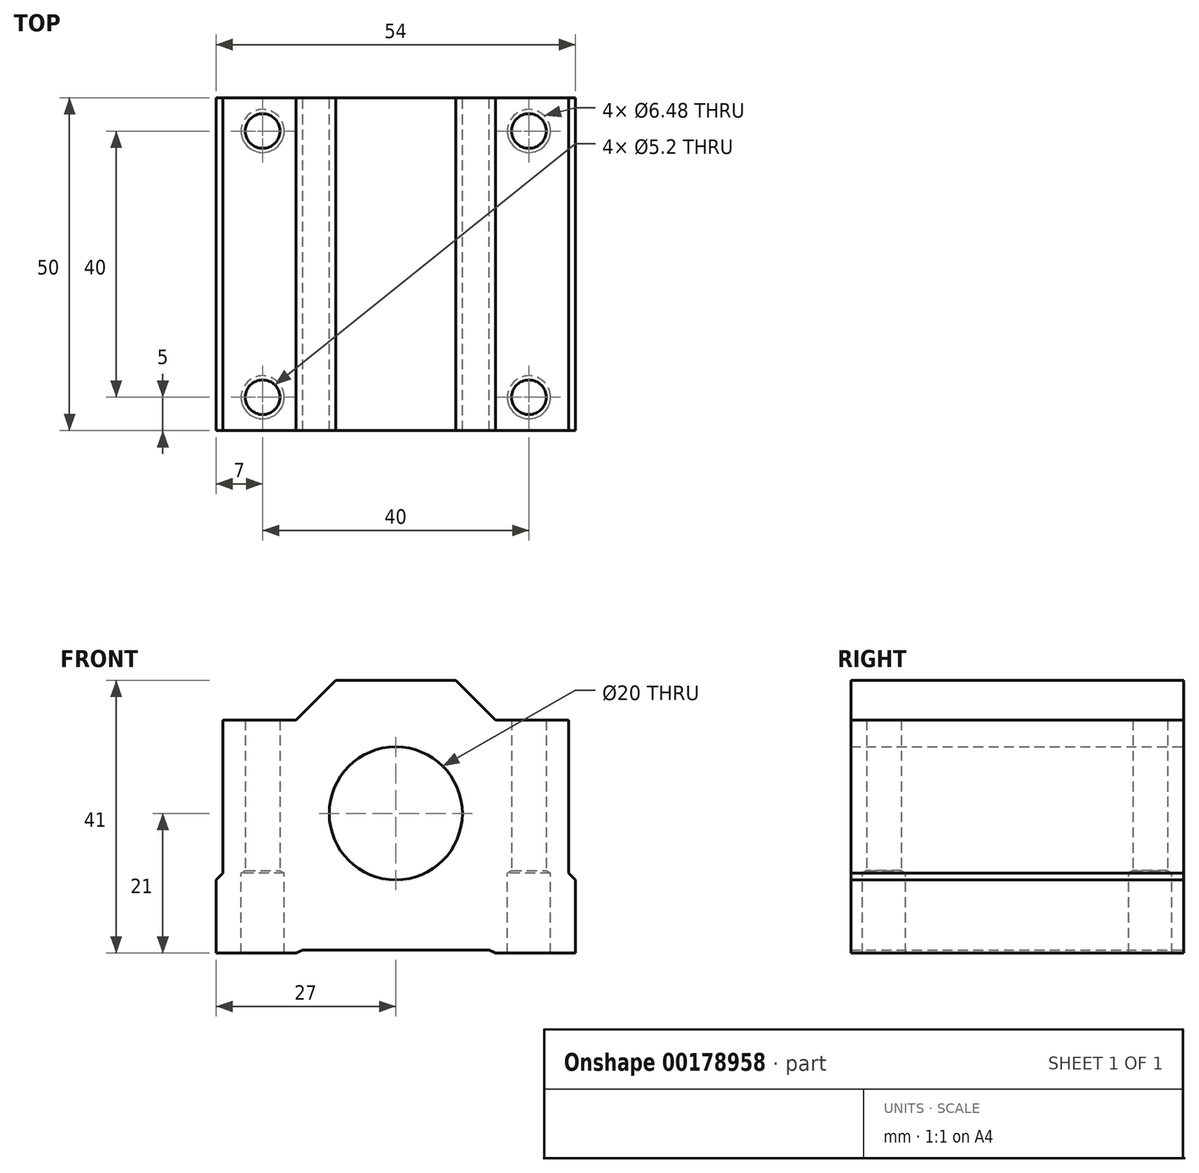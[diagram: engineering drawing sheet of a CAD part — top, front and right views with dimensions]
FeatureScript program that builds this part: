
annotation { "Feature Type Name" : "Feature", "Feature Type Description" : "" }
export const myFeature = defineFeature(function(context is Context, id is Id, definition is map)
    precondition{}
    {
        {
            var Q0;
            Q0=qCreatedBy(makeId("Front.planeOp"),FACE);
            var sketch = newSketch(context, id + "F0", { "sketchPlane" : qUnion([Q0])});
            skLineSegment(sketch, "E0.bottom", {"start": v(27, -20.5) * mm, "end": v(15, -20.5) * mm});
            skLineSegment(sketch, "E0.top", {"start": v(9, 20.5) * mm, "end": v(-9, 20.5) * mm});
            skLineSegment(sketch, "E0.left", {"start": v(27, -20.5) * mm, "end": v(27, -9.5) * mm});
            skLineSegment(sketch, "E0.right", {"start": v(-27, -20.5) * mm, "end": v(-27, -9.5) * mm});
            skPoint(sketch, "E0.middle", {"position": v(0, 0) * mm});
            skCircle(sketch, "E1", {"center": v(0, 0.5) * mm, "radius": 10 * mm});
            skLineSegment(sketch, "E2", {"start": v(-27, 14.5) * mm, "end": v(-15, 14.5) * mm});
            skLineSegment(sketch, "E3", {"start": v(-26, 14.5) * mm, "end": v(-26, -8.5) * mm});
            skLineSegment(sketch, "E4", {"start": v(26, 14.5) * mm, "end": v(26, -8.5) * mm});
            skLineSegment(sketch, "E5", {"start": v(-27, -9.5) * mm, "end": v(-26, -8.5) * mm});
            skLineSegment(sketch, "E6", {"start": v(27, -9.5) * mm, "end": v(26, -8.5) * mm});
            skLineSegment(sketch, "E7", {"start": v(-9, 20.5) * mm, "end": v(-15, 14.5) * mm});
            skLineSegment(sketch, "E8", {"start": v(9, 20.5) * mm, "end": v(15, 14.5) * mm});
            skPoint(sketch, "E9.trimOffspring.end.orphan", {"position": v(-27, 20.5) * mm});
            skPoint(sketch, "E9.trimOffspring.start.orphan", {"position": v(-26, 20.5) * mm});
            skPoint(sketch, "E10.orphan", {"position": v(-27, 0.5) * mm});
            skPoint(sketch, "E11.orphan", {"position": v(-27, -8.5) * mm});
            skPoint(sketch, "E12.orphan", {"position": v(27, 0.5) * mm});
            skLineSegment(sketch, "E13.trimOffspring", {"start": v(0, 0.5) * mm, "end": v(0, 0) * mm});
            skPoint(sketch, "E14.orphan", {"position": v(26, 20.5) * mm});
            skPoint(sketch, "E15.orphan", {"position": v(27, 20.5) * mm});
            skPoint(sketch, "E16.orphan", {"position": v(27, 14.5) * mm});
            skLineSegment(sketch, "E17.trimOffspring", {"start": v(15, 14.5) * mm, "end": v(26, 14.5) * mm});
            skPoint(sketch, "E18.start.orphan", {"position": v(0, 20.5) * mm});
            skPoint(sketch, "E19.trimOffspring.end.orphan", {"position": v(0, -20.5) * mm});
            skLineSegment(sketch, "E20", {"start": v(-14, -20) * mm, "end": v(14, -20) * mm});
            skLineSegment(sketch, "E21", {"start": v(-15, -20.5) * mm, "end": v(-14, -20) * mm});
            skLineSegment(sketch, "E22", {"start": v(15, -20.5) * mm, "end": v(14, -20) * mm});
            skPoint(sketch, "E23.orphan", {"position": v(-27, -20) * mm});
            skLineSegment(sketch, "E24.trimOffspring", {"start": v(-15, -20.5) * mm, "end": v(-27, -20.5) * mm});
            skPoint(sketch, "E25.end.orphan", {"position": v(-14, -20.5) * mm});
            skPoint(sketch, "E26.end.orphan", {"position": v(14, -20.5) * mm});
            skSolve(sketch);
        }
        {
            var Q0;
            Q0=makeQuery(id+"F0.imprint","IMPRINT",FACE,{"disambiguationData":[TD([[makeQuery(id+"F0.imprint","IMPRINT",EDGE,{"derivedFrom":sQuery(id+"F0.wireOp",EDGE,"E0.bottom")}),-1.0]])]});
            extrude(context, id + "F1", {"entities" : qUnion([Q0]), "depth" : 50 * mm});
        }
        {
            var Q0;
            Q0=makeQuery(id+"F1.opExtrude","SWEPT_FACE",FACE,{"disambiguationData":[OSD([sQuery(id+"F0.wireOp",EDGE,"E0.bottom")])]});
            var sketch = newSketch(context, id + "F2", { "sketchPlane" : qUnion([Q0])});
            skCircle(sketch, "E27", {"center": v(20, 5) * mm, "radius": 3.24 * mm});
            skCircle(sketch, "E28", {"center": v(-20, 5) * mm, "radius": 3.24 * mm});
            skCircle(sketch, "E29", {"center": v(20, 45) * mm, "radius": 3.24 * mm});
            skCircle(sketch, "E30", {"center": v(-20, 45) * mm, "radius": 3.24 * mm});
            skPoint(sketch, "E31.start.orphan", {"position": v(27, 5) * mm});
            skPoint(sketch, "E32.start.orphan", {"position": v(27, 45) * mm});
            skPoint(sketch, "E33.orphan", {"position": v(20, 50) * mm});
            skPoint(sketch, "E34.start.orphan", {"position": v(34, 50) * mm});
            skPoint(sketch, "E35.trimOffspring.end.orphan", {"position": v(-27, 45) * mm});
            skPoint(sketch, "E36.orphan", {"position": v(-27, 5) * mm});
            skSolve(sketch);
        }
        {
            var Q0;
            Q0=makeQuery(id+"F1.opExtrude","SWEPT_FACE",FACE,{"disambiguationData":[OSD([sQuery(id+"F0.wireOp",EDGE,"E2")])]});
            var sketch = newSketch(context, id + "F3", { "sketchPlane" : qUnion([Q0])});
            skCircle(sketch, "E37", {"center": v(-20, -45) * mm, "radius": 2.6 * mm});
            skCircle(sketch, "E38", {"center": v(-20, -5) * mm, "radius": 2.6 * mm});
            skPoint(sketch, "E39.orphan", {"position": v(-26, -5) * mm});
            skPoint(sketch, "E40.start.orphan", {"position": v(-20, 0) * mm});
            skPoint(sketch, "E41.start.orphan", {"position": v(-26, -45) * mm});
            skSolve(sketch);
        }
        {
            var Q0;
            Q0=makeQuery(id+"F1.opExtrude","SWEPT_FACE",FACE,{"disambiguationData":[OSD([sQuery(id+"F0.wireOp",EDGE,"E17.trimOffspring")])]});
            var sketch = newSketch(context, id + "F4", { "sketchPlane" : qUnion([Q0])});
            skCircle(sketch, "E42", {"center": v(20, -45) * mm, "radius": 2.6 * mm});
            skCircle(sketch, "E43", {"center": v(20, -5) * mm, "radius": 2.6 * mm});
            skPoint(sketch, "E44.orphan", {"position": v(20, -50) * mm});
            skPoint(sketch, "E45.trimOffspring.end.orphan", {"position": v(26, -45) * mm});
            skPoint(sketch, "E46.trimOffspring.end.orphan", {"position": v(26, -5) * mm});
            skSolve(sketch);
        }
        {
            var Q0;
            Q0=sQuery(id+"F2.wireOp",VERTEX,"E29.center");
            var Q1;
            Q1=makeQuery(id+"F1.opExtrude","SWEPT_BODY",BODY,{"disambiguationData":[OSD([sQuery(id+"F0.wireOp",EDGE,"E0.bottom"),sQuery(id+"F0.wireOp",EDGE,"E0.top"),sQuery(id+"F0.wireOp",EDGE,"E0.left"),sQuery(id+"F0.wireOp",EDGE,"E0.right"),sQuery(id+"F0.wireOp",EDGE,"E1"),sQuery(id+"F0.wireOp",EDGE,"E2"),sQuery(id+"F0.wireOp",EDGE,"E3"),sQuery(id+"F0.wireOp",EDGE,"E4"),sQuery(id+"F0.wireOp",EDGE,"E5"),sQuery(id+"F0.wireOp",EDGE,"E6"),sQuery(id+"F0.wireOp",EDGE,"E7"),sQuery(id+"F0.wireOp",EDGE,"E8"),sQuery(id+"F0.wireOp",EDGE,"E17.trimOffspring")])]});
            hole(context, id + "F5", {"style" : HoleStyle.SIMPLE, "endStyle" : HoleEndStyle.BLIND, "holeDiameter" : 6.48 * mm, "holeDepth" : 12 * mm, "locations" : qUnion([Q0]), "scope" : qUnion([Q1])});
        }
        {
            var Q0;
            Q0=sQuery(id+"F2.wireOp",VERTEX,"E30.center");
            var Q1;
            Q1=makeQuery(id+"F1.opExtrude","SWEPT_BODY",BODY,{"disambiguationData":[OSD([sQuery(id+"F0.wireOp",EDGE,"E0.bottom"),sQuery(id+"F0.wireOp",EDGE,"E0.top"),sQuery(id+"F0.wireOp",EDGE,"E0.left"),sQuery(id+"F0.wireOp",EDGE,"E0.right"),sQuery(id+"F0.wireOp",EDGE,"E1"),sQuery(id+"F0.wireOp",EDGE,"E2"),sQuery(id+"F0.wireOp",EDGE,"E3"),sQuery(id+"F0.wireOp",EDGE,"E4"),sQuery(id+"F0.wireOp",EDGE,"E5"),sQuery(id+"F0.wireOp",EDGE,"E6"),sQuery(id+"F0.wireOp",EDGE,"E7"),sQuery(id+"F0.wireOp",EDGE,"E8"),sQuery(id+"F0.wireOp",EDGE,"E17.trimOffspring")])]});
            hole(context, id + "F6", {"style" : HoleStyle.SIMPLE, "endStyle" : HoleEndStyle.BLIND, "holeDiameter" : 6.48 * mm, "holeDepth" : 12 * mm, "locations" : qUnion([Q0]), "scope" : qUnion([Q1])});
        }
        {
            var Q0;
            Q0=sQuery(id+"F2.wireOp",VERTEX,"E27.center");
            var Q1;
            Q1=makeQuery(id+"F1.opExtrude","SWEPT_BODY",BODY,{"disambiguationData":[OSD([sQuery(id+"F0.wireOp",EDGE,"E0.bottom"),sQuery(id+"F0.wireOp",EDGE,"E0.top"),sQuery(id+"F0.wireOp",EDGE,"E0.left"),sQuery(id+"F0.wireOp",EDGE,"E0.right"),sQuery(id+"F0.wireOp",EDGE,"E1"),sQuery(id+"F0.wireOp",EDGE,"E2"),sQuery(id+"F0.wireOp",EDGE,"E3"),sQuery(id+"F0.wireOp",EDGE,"E4"),sQuery(id+"F0.wireOp",EDGE,"E5"),sQuery(id+"F0.wireOp",EDGE,"E6"),sQuery(id+"F0.wireOp",EDGE,"E7"),sQuery(id+"F0.wireOp",EDGE,"E8"),sQuery(id+"F0.wireOp",EDGE,"E17.trimOffspring")])]});
            hole(context, id + "F7", {"style" : HoleStyle.SIMPLE, "endStyle" : HoleEndStyle.BLIND, "holeDiameter" : 6.48 * mm, "holeDepth" : 12 * mm, "locations" : qUnion([Q0]), "scope" : qUnion([Q1])});
        }
        {
            var Q0;
            Q0=sQuery(id+"F2.wireOp",VERTEX,"E28.center");
            var Q1;
            Q1=makeQuery(id+"F1.opExtrude","SWEPT_BODY",BODY,{"disambiguationData":[OSD([sQuery(id+"F0.wireOp",EDGE,"E0.bottom"),sQuery(id+"F0.wireOp",EDGE,"E0.top"),sQuery(id+"F0.wireOp",EDGE,"E0.left"),sQuery(id+"F0.wireOp",EDGE,"E0.right"),sQuery(id+"F0.wireOp",EDGE,"E1"),sQuery(id+"F0.wireOp",EDGE,"E2"),sQuery(id+"F0.wireOp",EDGE,"E3"),sQuery(id+"F0.wireOp",EDGE,"E4"),sQuery(id+"F0.wireOp",EDGE,"E5"),sQuery(id+"F0.wireOp",EDGE,"E6"),sQuery(id+"F0.wireOp",EDGE,"E7"),sQuery(id+"F0.wireOp",EDGE,"E8"),sQuery(id+"F0.wireOp",EDGE,"E17.trimOffspring")])]});
            hole(context, id + "F8", {"style" : HoleStyle.SIMPLE, "endStyle" : HoleEndStyle.BLIND, "holeDiameter" : 6.48 * mm, "holeDepth" : 12 * mm, "locations" : qUnion([Q0]), "scope" : qUnion([Q1])});
        }
        {
            var Q0;
            Q0=sQuery(id+"F4.wireOp",VERTEX,"E42.center");
            var Q1;
            Q1=makeQuery(id+"F1.opExtrude","SWEPT_BODY",BODY,{"disambiguationData":[OSD([sQuery(id+"F0.wireOp",EDGE,"E0.bottom"),sQuery(id+"F0.wireOp",EDGE,"E0.top"),sQuery(id+"F0.wireOp",EDGE,"E0.left"),sQuery(id+"F0.wireOp",EDGE,"E0.right"),sQuery(id+"F0.wireOp",EDGE,"E1"),sQuery(id+"F0.wireOp",EDGE,"E2"),sQuery(id+"F0.wireOp",EDGE,"E3"),sQuery(id+"F0.wireOp",EDGE,"E4"),sQuery(id+"F0.wireOp",EDGE,"E5"),sQuery(id+"F0.wireOp",EDGE,"E6"),sQuery(id+"F0.wireOp",EDGE,"E7"),sQuery(id+"F0.wireOp",EDGE,"E8"),sQuery(id+"F0.wireOp",EDGE,"E17.trimOffspring")])]});
            hole(context, id + "F9", {"style" : HoleStyle.SIMPLE, "endStyle" : HoleEndStyle.BLIND, "holeDiameter" : 5.2 * mm, "holeDepth" : 23 * mm, "locations" : qUnion([Q0]), "scope" : qUnion([Q1])});
        }
        {
            var Q0;
            Q0=sQuery(id+"F3.wireOp",VERTEX,"E37.center");
            var Q1;
            Q1=makeQuery(id+"F1.opExtrude","SWEPT_BODY",BODY,{"disambiguationData":[OSD([sQuery(id+"F0.wireOp",EDGE,"E0.bottom"),sQuery(id+"F0.wireOp",EDGE,"E0.top"),sQuery(id+"F0.wireOp",EDGE,"E0.left"),sQuery(id+"F0.wireOp",EDGE,"E0.right"),sQuery(id+"F0.wireOp",EDGE,"E1"),sQuery(id+"F0.wireOp",EDGE,"E2"),sQuery(id+"F0.wireOp",EDGE,"E3"),sQuery(id+"F0.wireOp",EDGE,"E4"),sQuery(id+"F0.wireOp",EDGE,"E5"),sQuery(id+"F0.wireOp",EDGE,"E6"),sQuery(id+"F0.wireOp",EDGE,"E7"),sQuery(id+"F0.wireOp",EDGE,"E8"),sQuery(id+"F0.wireOp",EDGE,"E17.trimOffspring")])]});
            hole(context, id + "F10", {"style" : HoleStyle.SIMPLE, "endStyle" : HoleEndStyle.BLIND, "holeDiameter" : 5.2 * mm, "holeDepth" : 23 * mm, "locations" : qUnion([Q0]), "scope" : qUnion([Q1])});
        }
        {
            var Q0;
            Q0=sQuery(id+"F3.wireOp",VERTEX,"E38.center");
            var Q1;
            Q1=makeQuery(id+"F1.opExtrude","SWEPT_BODY",BODY,{"disambiguationData":[OSD([sQuery(id+"F0.wireOp",EDGE,"E0.bottom"),sQuery(id+"F0.wireOp",EDGE,"E0.top"),sQuery(id+"F0.wireOp",EDGE,"E0.left"),sQuery(id+"F0.wireOp",EDGE,"E0.right"),sQuery(id+"F0.wireOp",EDGE,"E1"),sQuery(id+"F0.wireOp",EDGE,"E2"),sQuery(id+"F0.wireOp",EDGE,"E3"),sQuery(id+"F0.wireOp",EDGE,"E4"),sQuery(id+"F0.wireOp",EDGE,"E5"),sQuery(id+"F0.wireOp",EDGE,"E6"),sQuery(id+"F0.wireOp",EDGE,"E7"),sQuery(id+"F0.wireOp",EDGE,"E8"),sQuery(id+"F0.wireOp",EDGE,"E17.trimOffspring")])]});
            hole(context, id + "F11", {"style" : HoleStyle.SIMPLE, "endStyle" : HoleEndStyle.BLIND, "holeDiameter" : 5.2 * mm, "holeDepth" : 23 * mm, "locations" : qUnion([Q0]), "scope" : qUnion([Q1])});
        }
        {
            var Q0;
            Q0=sQuery(id+"F4.wireOp",VERTEX,"E43.center");
            var Q1;
            Q1=makeQuery(id+"F1.opExtrude","SWEPT_BODY",BODY,{"disambiguationData":[OSD([sQuery(id+"F0.wireOp",EDGE,"E0.bottom"),sQuery(id+"F0.wireOp",EDGE,"E0.top"),sQuery(id+"F0.wireOp",EDGE,"E0.left"),sQuery(id+"F0.wireOp",EDGE,"E0.right"),sQuery(id+"F0.wireOp",EDGE,"E1"),sQuery(id+"F0.wireOp",EDGE,"E2"),sQuery(id+"F0.wireOp",EDGE,"E3"),sQuery(id+"F0.wireOp",EDGE,"E4"),sQuery(id+"F0.wireOp",EDGE,"E5"),sQuery(id+"F0.wireOp",EDGE,"E6"),sQuery(id+"F0.wireOp",EDGE,"E7"),sQuery(id+"F0.wireOp",EDGE,"E8"),sQuery(id+"F0.wireOp",EDGE,"E17.trimOffspring")])]});
            hole(context, id + "F12", {"style" : HoleStyle.SIMPLE, "endStyle" : HoleEndStyle.BLIND, "holeDiameter" : 5.2 * mm, "holeDepth" : 23 * mm, "locations" : qUnion([Q0]), "scope" : qUnion([Q1])});
        }
    });
